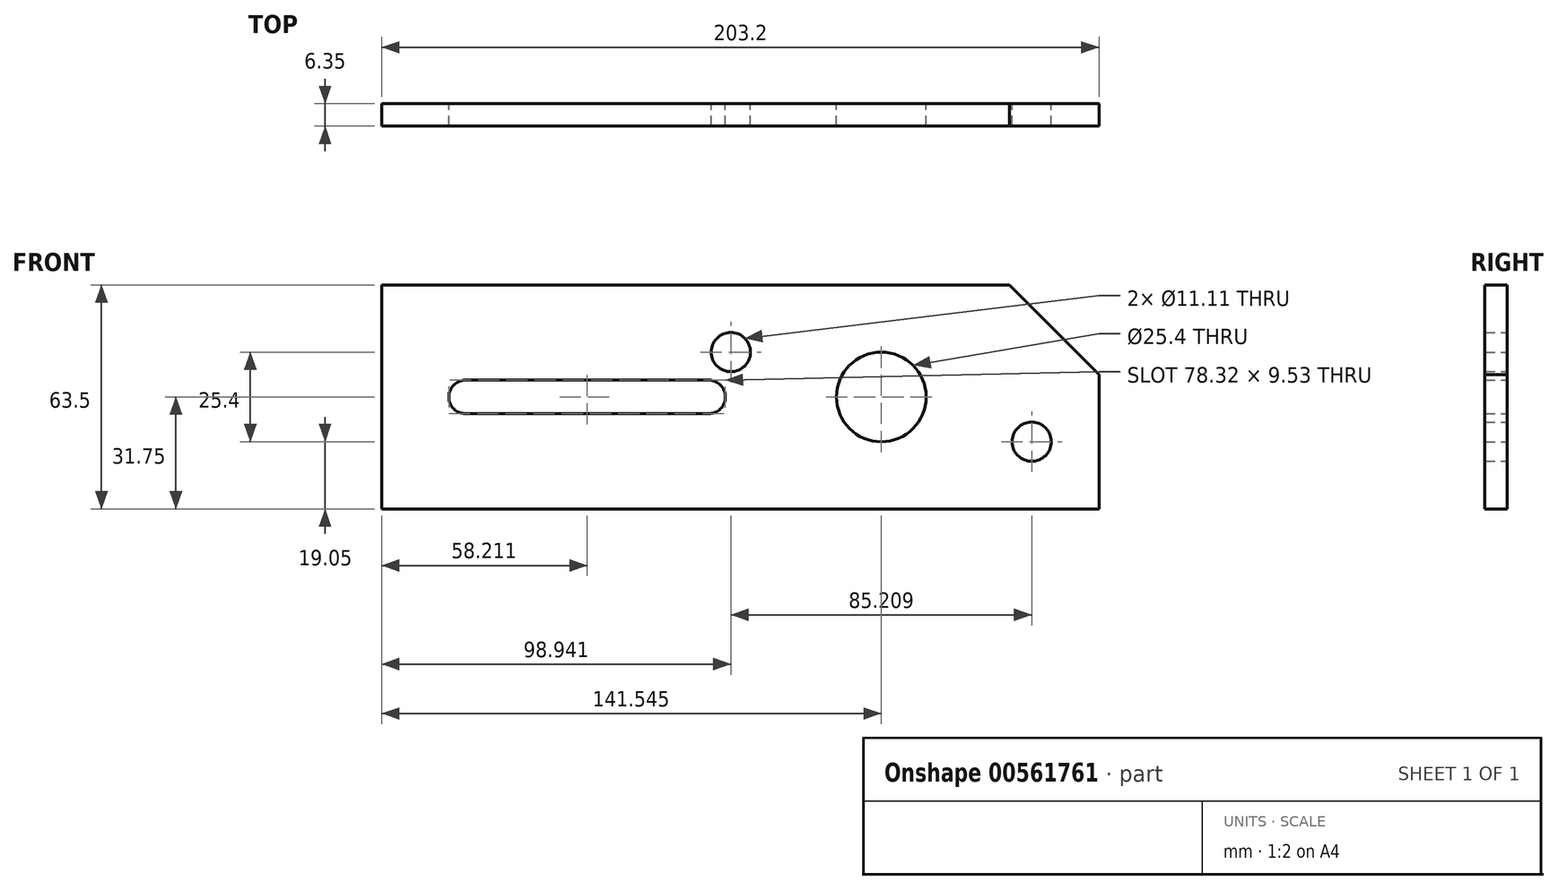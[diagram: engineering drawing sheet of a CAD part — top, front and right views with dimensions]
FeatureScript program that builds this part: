
annotation { "Feature Type Name" : "Feature", "Feature Type Description" : "" }
export const myFeature = defineFeature(function(context is Context, id is Id, definition is map)
    precondition{}
    {
        {
            var Q0;
            Q0=qCreatedBy(makeId("Front.planeOp"),FACE);
            var sketch = newSketch(context, id + "F0", { "sketchPlane" : qUnion([Q0])});
            skLineSegment(sketch, "E0.bottom", {"start": v(101.6, -31.75) * mm, "end": v(-101.6, -31.75) * mm});
            skLineSegment(sketch, "E0.top", {"start": v(76.2, 31.75) * mm, "end": v(-101.6, 31.75) * mm});
            skLineSegment(sketch, "E0.left", {"start": v(101.6, -31.75) * mm, "end": v(101.6, 6.35) * mm});
            skLineSegment(sketch, "E0.right", {"start": v(-101.6, -31.75) * mm, "end": v(-101.6, 31.75) * mm});
            skPoint(sketch, "E0.middle", {"position": v(0, 0) * mm});
            skLineSegment(sketch, "E1", {"start": v(76.2, 31.75) * mm, "end": v(101.6, 6.35) * mm});
            skPoint(sketch, "E2.orphan", {"position": v(101.6, 31.75) * mm});
            skArc(sketch, "E3", {"start": v(-77.79, 4.76) * mm, "mid": v(-82.55, 0) * mm, "end": v(-77.79, -4.76) * mm});
            skPoint(sketch, "E3.centerSnap0", {"position": v(-101.6, 0) * mm});
            skLineSegment(sketch, "E4", {"start": v(-77.79, 4.76) * mm, "end": v(-8.99, 4.76) * mm});
            skLineSegment(sketch, "E5", {"start": v(-8.99, -4.76) * mm, "end": v(-77.79, -4.76) * mm});
            skCircle(sketch, "E6", {"center": v(82.55, -12.7) * mm, "radius": 5.56 * mm});
            skCircle(sketch, "E7", {"center": v(-2.66, 12.7) * mm, "radius": 5.56 * mm});
            skArc(sketch, "E8", {"start": v(-8.99, 4.76) * mm, "mid": v(-4.23, 0) * mm, "end": v(-8.99, -4.76) * mm});
            skLineSegment(sketch, "E9", {"start": v(-2.66, 12.7) * mm, "end": v(82.55, -12.7) * mm});
            skCircle(sketch, "E10", {"center": v(39.95, 0) * mm, "radius": 12.7 * mm});
            skPoint(sketch, "E11", {"position": v(-82.55, 0) * mm});
            skPoint(sketch, "E12", {"position": v(-4.23, 0) * mm});
            skLineSegment(sketch, "E13", {"start": v(-82.55, 0) * mm, "end": v(-82.54, 0.3) * mm});
            skLineSegment(sketch, "E14", {"start": v(-4.23, 0) * mm, "end": v(-4.23, 0.22) * mm});
            skSolve(sketch);
        }
        {
            var Q0;
            Q0=makeQuery(id+"F0.imprint","IMPRINT",FACE,{"disambiguationData":[TD([[makeQuery(id+"F0.imprint","IMPRINT",EDGE,{"derivedFrom":sQuery(id+"F0.wireOp",EDGE,"E0.bottom")}),-1.0]])]});
            extrude(context, id + "F1", {"entities" : qUnion([Q0]), "depth" : 6.35 * mm, "offsetDistance" : 25.4 * mm});
        }
    });
